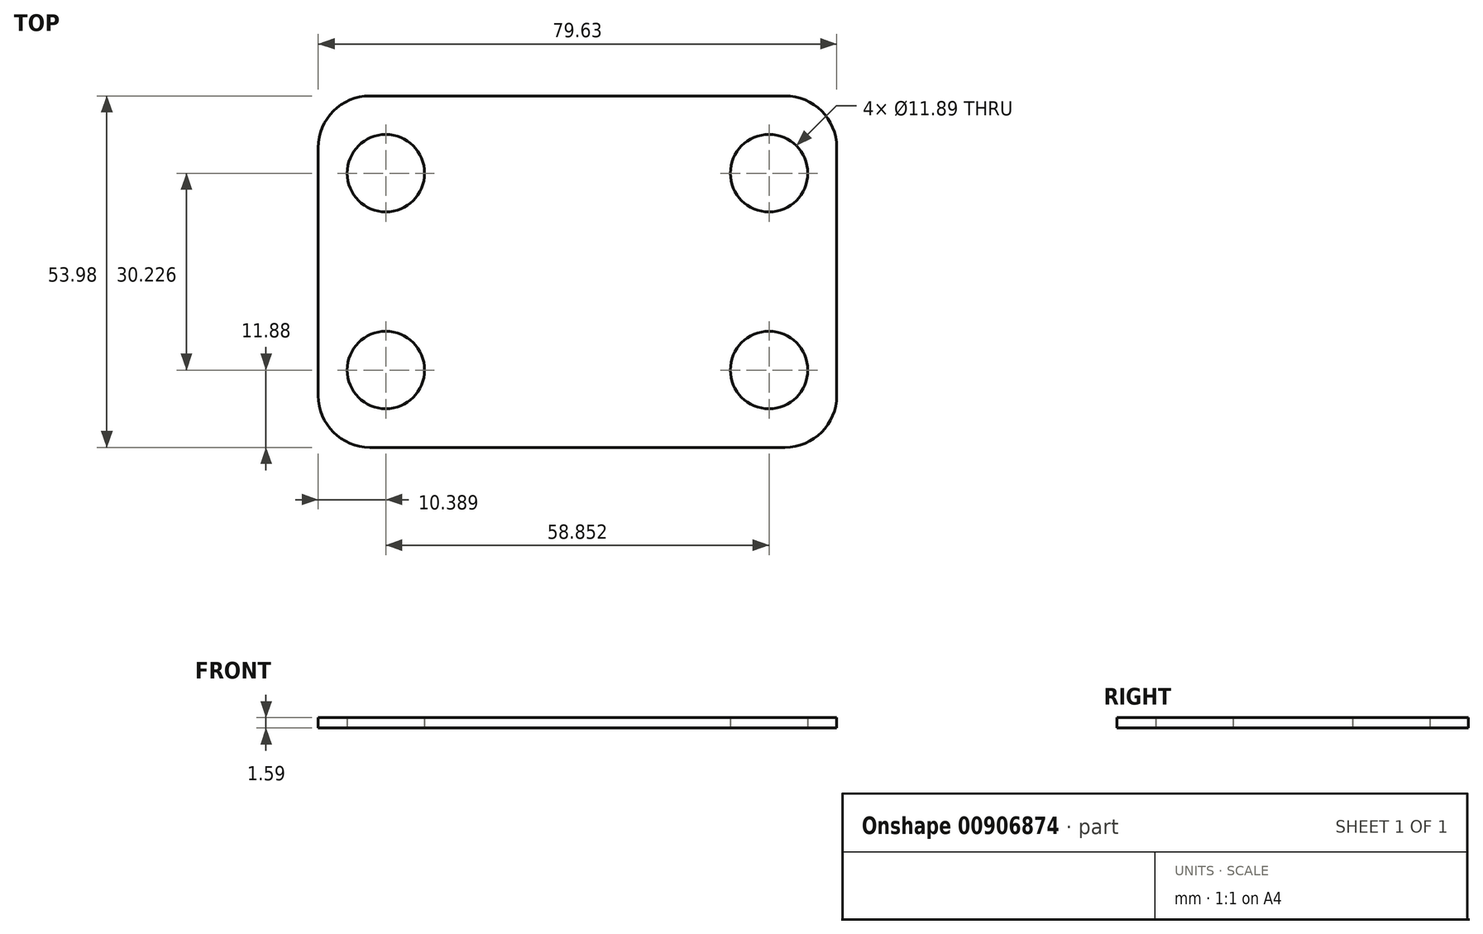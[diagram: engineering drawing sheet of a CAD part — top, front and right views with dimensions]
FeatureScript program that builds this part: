
annotation { "Feature Type Name" : "Feature", "Feature Type Description" : "" }
export const myFeature = defineFeature(function(context is Context, id is Id, definition is map)
    precondition{}
    {
        {
            var Q0;
            Q0=qCreatedBy(makeId("Top.planeOp"),FACE);
            var sketch = newSketch(context, id + "F0", { "sketchPlane" : qUnion([Q0])});
            skLineSegment(sketch, "E0.bottom", {"start": v(7.94, 0) * mm, "end": v(71.7, 0) * mm});
            skLineSegment(sketch, "E0.top", {"start": v(7.94, -53.97) * mm, "end": v(71.7, -53.97) * mm});
            skLineSegment(sketch, "E0.left", {"start": v(0, -7.94) * mm, "end": v(0, -46.04) * mm});
            skLineSegment(sketch, "E0.right", {"start": v(79.63, -7.94) * mm, "end": v(79.63, -46.04) * mm});
            skLineSegment(sketch, "E1", {"start": v(39.81, 0) * mm, "end": v(39.81, -53.97) * mm, "construction": true});
            skLineSegment(sketch, "E2", {"start": v(79.63, -26.99) * mm, "end": v(0, -26.99) * mm, "construction": true});
            skCircle(sketch, "E3", {"center": v(10.39, -11.87) * mm, "radius": 5.94 * mm});
            skCircle(sketch, "E4", {"center": v(69.24, -11.87) * mm, "radius": 5.94 * mm});
            skCircle(sketch, "E5", {"center": v(69.24, -42.1) * mm, "radius": 5.94 * mm});
            skCircle(sketch, "E6", {"center": v(10.39, -42.1) * mm, "radius": 5.94 * mm});
            skPoint(sketch, "E7.visualSharp", {"position": v(0, 0) * mm});
            skArc(sketch, "E7.filletArc", {"start": v(7.94, 0) * mm, "mid": v(2.32, -2.32) * mm, "end": v(0, -7.94) * mm});
            skPoint(sketch, "E8.visualSharp", {"position": v(7.94, 0) * mm});
            skLineSegment(sketch, "E8.filletArc", {"start": v(7.94, 0) * mm, "end": v(7.94, 0) * mm});
            skPoint(sketch, "E9.visualSharp", {"position": v(79.63, 0) * mm});
            skArc(sketch, "E9.filletArc", {"start": v(79.63, -7.94) * mm, "mid": v(77.3, -2.32) * mm, "end": v(71.7, 0) * mm});
            skPoint(sketch, "E10.visualSharp", {"position": v(79.63, -53.97) * mm});
            skArc(sketch, "E10.filletArc", {"start": v(71.7, -53.97) * mm, "mid": v(77.3, -51.65) * mm, "end": v(79.63, -46.04) * mm});
            skPoint(sketch, "E11.visualSharp", {"position": v(0, -53.97) * mm});
            skArc(sketch, "E11.filletArc", {"start": v(0, -46.04) * mm, "mid": v(2.32, -51.65) * mm, "end": v(7.94, -53.97) * mm});
            skSolve(sketch);
        }
        {
            var Q0;
            Q0 = qSketchRegion(id + "F0", true);
            extrude(context, id + "F1", {"entities" : qUnion([Q0]), "depth" : 1.59 * mm, "offsetDistance" : 25.4 * mm});
        }
    });
